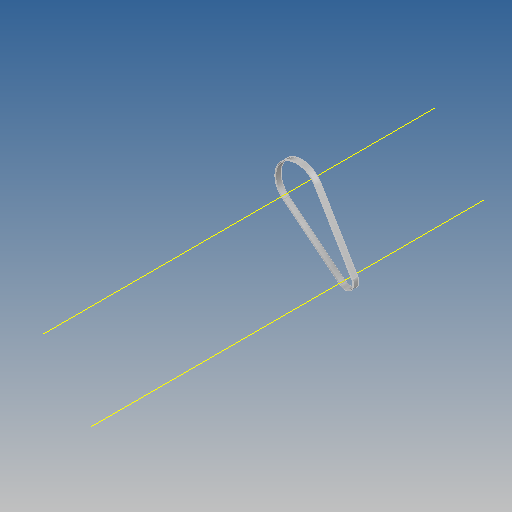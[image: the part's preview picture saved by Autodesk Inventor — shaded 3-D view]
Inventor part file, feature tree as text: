
AUTODESK INVENTOR PART (.ipt)
format: ipt  version: 2020 (Build 240168000, 168)  size: 100,352 bytes
history: native  units: mm (DEFAULTED — no unit token found)
features: other x4, plane x2, sketch x1, sweep x1
ambient origin geometry x8: Origin, YZ Plane, XZ Plane, XY Plane, X Axis, Y Axis, Z Axis, Center Point
bodies: Solid1 (feature_tree)
feature tree (8):
  sketch  "Sketch Path"  dims[d0=4.0mm d2=0.0mm d4=0.3mm d5=0.3mm d6=0.0mm d7=0.0mm d8=0.0mm d9=0.0mm d10=0.0mm d11=0.0mm]
  other  "Cross Section Plane"
  other  "Work Axis1"
  other  "Work Axis2"
  plane  "Work Plane2"
  plane  "Work Plane3"
  sweep  "Belt"
  other  "Cross Section"
